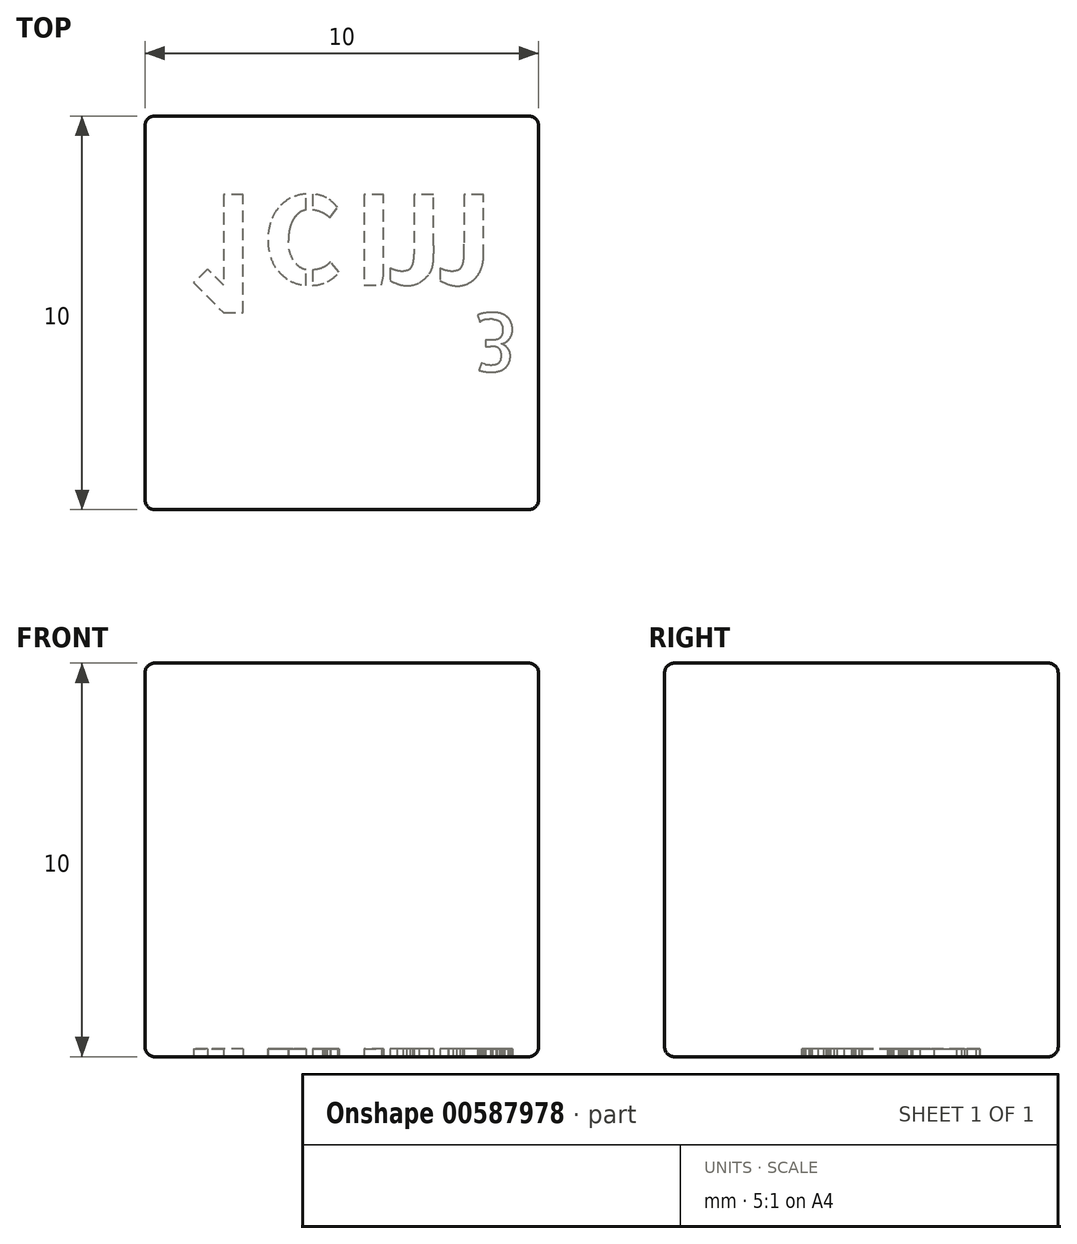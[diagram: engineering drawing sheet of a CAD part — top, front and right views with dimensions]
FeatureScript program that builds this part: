
annotation { "Feature Type Name" : "Feature", "Feature Type Description" : "" }
export const myFeature = defineFeature(function(context is Context, id is Id, definition is map)
    precondition{}
    {
        {
            var Q0;
            Q0=qCreatedBy(makeId("Top.planeOp"),FACE);
            var sketch = newSketch(context, id + "F0", { "sketchPlane" : qUnion([Q0])});
            skLineSegment(sketch, "E0.bottom", {"start": v(-5, 5) * mm, "end": v(5, 5) * mm});
            skLineSegment(sketch, "E0.top", {"start": v(-5, -5) * mm, "end": v(5, -5) * mm});
            skLineSegment(sketch, "E0.left", {"start": v(-5, 5) * mm, "end": v(-5, -5) * mm});
            skLineSegment(sketch, "E0.right", {"start": v(5, 5) * mm, "end": v(5, -5) * mm});
            skPoint(sketch, "E0.middle", {"position": v(0, 0) * mm});
            skText(sketch, "E1", { "text": "1cm", "fontName": "OpenSans-Regular.ttf"});
            skText(sketch, "E2", { "text": "3", "fontName": "OpenSans-Regular.ttf"});
            const initialGuessF0  = {"E1": [-0.0035, -0.00128, 1, 0, 0.00257], "E2": [0.0029, 0.00128, 1, 0, 0.0015]};
            skSetInitialGuess(sketch, initialGuessF0);
            skSolve(sketch);
        }
        {
            var Q0;
            Q0=makeQuery(id+"F0.imprint","IMPRINT",FACE,{"disambiguationData":[TD([[makeQuery(id+"F0.imprint","IMPRINT",EDGE,{"derivedFrom":sQuery(id+"F0.wireOp",EDGE,"E1.sketch_text.stroke-9")}),-1.0]])]});
            var Q1;
            Q1=makeQuery(id+"F0.imprint","IMPRINT",FACE,{"disambiguationData":[TD([[makeQuery(id+"F0.imprint","IMPRINT",EDGE,{"derivedFrom":sQuery(id+"F0.wireOp",EDGE,"E1.sketch_text.stroke-24")}),-1.0]])]});
            var Q2;
            Q2=makeQuery(id+"F0.imprint","IMPRINT",FACE,{"disambiguationData":[TD([[makeQuery(id+"F0.imprint","IMPRINT",EDGE,{"derivedFrom":sQuery(id+"F0.wireOp",EDGE,"E1.sketch_text.stroke-0")}),-1.0]])]});
            var Q3;
            Q3=makeQuery(id+"F0.imprint","IMPRINT",FACE,{"disambiguationData":[TD([[makeQuery(id+"F0.imprint","IMPRINT",EDGE,{"derivedFrom":sQuery(id+"F0.wireOp",EDGE,"E2.sketch_text.stroke-0")}),-1.0]])]});
            var Q4;
            Q4=makeQuery(id+"F0.imprint","IMPRINT",FACE,{"disambiguationData":[TD([[makeQuery(id+"F0.imprint","IMPRINT",EDGE,{"derivedFrom":sQuery(id+"F0.wireOp",EDGE,"E0.bottom")}),-1.0]])]});
            extrude(context, id + "F1", {"entities" : qUnion([Q0, Q1, Q2, Q3, Q4]), "depth" : 10 * mm, "offsetDistance" : 25 * mm});
        }
        {
            var Q0;
            Q0=makeQuery(id+"F1.opExtrude","CAP_FACE",FACE,{"disambiguationData":[OSD([sQuery(id+"F0.wireOp",EDGE,"E0.bottom"),sQuery(id+"F0.wireOp",EDGE,"E0.top"),sQuery(id+"F0.wireOp",EDGE,"E0.left"),sQuery(id+"F0.wireOp",EDGE,"E0.right")])],"isStart":true});
            var sketch = newSketch(context, id + "F2", { "sketchPlane" : qUnion([Q0])});
            skText(sketch, "E3", { "text": "1cm", "fontName": "AllertaStencil-Regular.ttf"});
            skText(sketch, "E4", { "text": "3", "fontName": "AllertaStencil-Regular.ttf"});
            const initialGuessF2  = {"E3": [-0.00388, -0.003, 1, 0, 0.003], "E4": [0.0033, 0, 1, 0, 0.0015]};
            skSetInitialGuess(sketch, initialGuessF2);
            skSolve(sketch);
        }
        {
            var Q0;
            Q0 = qSketchRegion(id + "F2", true);
            extrude(context, id + "F3", {"entities" : qUnion([Q0]), "operationType" : NewBodyOperationType.REMOVE, "oppositeDirection" : true, "depth" : .2 * mm, "offsetDistance" : 25 * mm});
        }
        {
            var Q0;
            Q0=makeQuery(id+"F1.opExtrude","CAP_FACE",FACE,{"disambiguationData":[OSD([sQuery(id+"F0.wireOp",EDGE,"E0.bottom"),sQuery(id+"F0.wireOp",EDGE,"E0.top"),sQuery(id+"F0.wireOp",EDGE,"E0.left"),sQuery(id+"F0.wireOp",EDGE,"E0.right")])],"isStart":false});
            var Q1;
            Q1=makeQuery(id+"F1.opExtrude","SWEPT_FACE",FACE,{"disambiguationData":[OSD([sQuery(id+"F0.wireOp",EDGE,"E0.right")])]});
            var Q2;
            Q2=makeQuery(id+"F1.opExtrude","SWEPT_FACE",FACE,{"disambiguationData":[OSD([sQuery(id+"F0.wireOp",EDGE,"E0.top")])]});
            var Q3;
            Q3=makeQuery(id+"F1.opExtrude","SWEPT_FACE",FACE,{"disambiguationData":[OSD([sQuery(id+"F0.wireOp",EDGE,"E0.bottom")])]});
            var Q4;
            Q4=makeQuery(id+"F1.opExtrude","SWEPT_FACE",FACE,{"disambiguationData":[OSD([sQuery(id+"F0.wireOp",EDGE,"E0.left")])]});
            fillet(context, id + "F4", {"entities" : qUnion([Q0, Q1, Q2, Q3, Q4]), "radius" : .25 * mm, "tangentPropagation" : true, "allowEdgeOverflow" : false});
        }
    });
